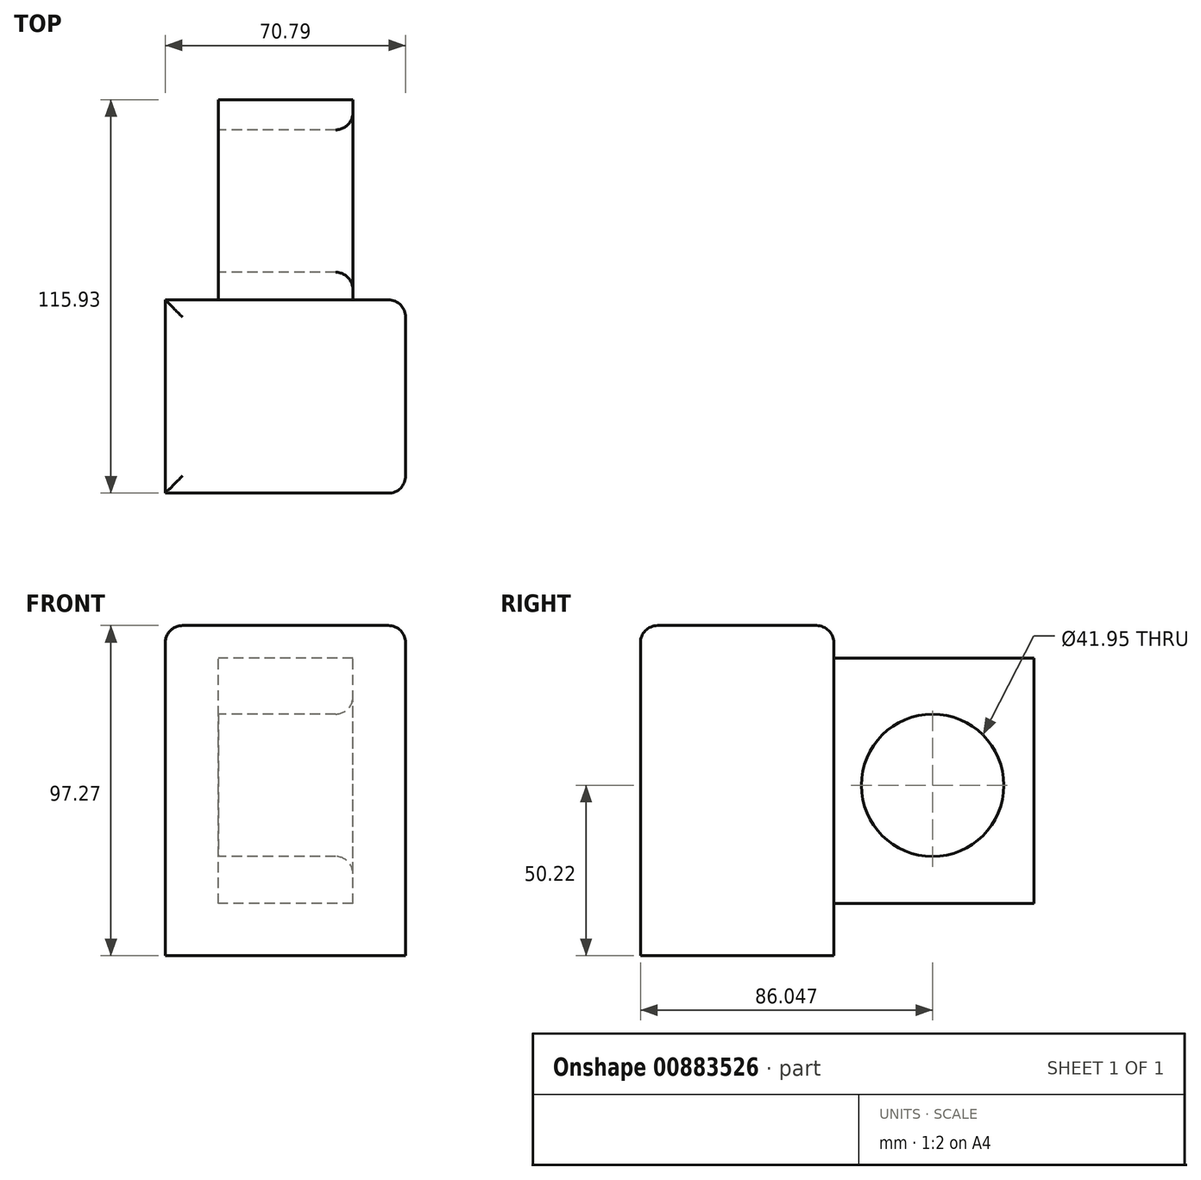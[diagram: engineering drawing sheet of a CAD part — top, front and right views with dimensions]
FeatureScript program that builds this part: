
annotation { "Feature Type Name" : "Feature", "Feature Type Description" : "" }
export const myFeature = defineFeature(function(context is Context, id is Id, definition is map)
    precondition{}
    {
        {
            var Q0;
            Q0=qCreatedBy(makeId("Top.planeOp"),FACE);
            var sketch = newSketch(context, id + "F0", { "sketchPlane" : qUnion([Q0])});
            skLineSegment(sketch, "E0.bottom", {"start": v(16.2, 0) * mm, "end": v(87, 0) * mm});
            skLineSegment(sketch, "E0.top", {"start": v(16.2, 56.94) * mm, "end": v(87, 56.94) * mm});
            skLineSegment(sketch, "E0.left", {"start": v(16.2, 0) * mm, "end": v(16.2, 56.94) * mm});
            skLineSegment(sketch, "E0.right", {"start": v(87, 0) * mm, "end": v(87, 56.94) * mm});
            skPoint(sketch, "E0.middle", {"position": v(51.6, 28.47) * mm});
            skSolve(sketch);
        }
        {
            var Q0;
            Q0=makeQuery(id+"F0.imprint","IMPRINT",FACE,{"disambiguationData":[TD([[makeQuery(id+"F0.imprint","IMPRINT",EDGE,{"derivedFrom":sQuery(id+"F0.wireOp",EDGE,"E0.bottom")}),1.0]])]});
            extrude(context, id + "F1", {"entities" : qUnion([Q0]), "depth" : 97.27 * mm, "offsetDistance" : 25.4 * mm});
        }
        {
            var Q0;
            Q0=makeQuery(id+"F1.opExtrude","CAP_EDGE",EDGE,{"disambiguationData":[OSD([sQuery(id+"F0.wireOp",EDGE,"E0.right")])],"isStart":false});
            fillet(context, id + "F2", {"entities" : qUnion([Q0]), "radius" : 5.08 * mm, "tangentPropagation" : true, "allowEdgeOverflow" : false});
        }
        {
            var Q0;
            Q0=makeQuery(id+"F1.opExtrude","CAP_EDGE",EDGE,{"disambiguationData":[OSD([sQuery(id+"F0.wireOp",EDGE,"E0.left")])],"isStart":false});
            var Q1;
            Q1=makeQuery(id+"F1.opExtrude","CAP_EDGE",EDGE,{"disambiguationData":[OSD([sQuery(id+"F0.wireOp",EDGE,"E0.bottom")])],"isStart":false});
            var Q2;
            Q2=makeQuery(id+"F1.opExtrude","CAP_EDGE",EDGE,{"disambiguationData":[OSD([sQuery(id+"F0.wireOp",EDGE,"E0.top")])],"isStart":false});
            fillet(context, id + "F3", {"entities" : qUnion([Q0, Q1, Q2]), "radius" : 5.08 * mm, "tangentPropagation" : true, "allowEdgeOverflow" : false});
        }
        {
            var Q0;
            Q0=makeQuery(id+"F1.opExtrude","SWEPT_FACE",FACE,{"disambiguationData":[OSD([sQuery(id+"F0.wireOp",EDGE,"E0.top")])]});
            var sketch = newSketch(context, id + "F4", { "sketchPlane" : qUnion([Q0])});
            skLineSegment(sketch, "E1.bottom", {"start": v(-71.47, 15.38) * mm, "end": v(-31.89, 15.38) * mm});
            skLineSegment(sketch, "E1.top", {"start": v(-71.47, 87.71) * mm, "end": v(-31.89, 87.71) * mm});
            skLineSegment(sketch, "E1.left", {"start": v(-71.47, 15.38) * mm, "end": v(-71.47, 87.71) * mm});
            skLineSegment(sketch, "E1.right", {"start": v(-31.89, 15.38) * mm, "end": v(-31.89, 87.71) * mm});
            skPoint(sketch, "E1.middle", {"position": v(-51.68, 51.55) * mm});
            skSolve(sketch);
        }
        {
            var Q0;
            Q0=makeQuery(id+"F4.imprint","IMPRINT",FACE,{"disambiguationData":[TD([[makeQuery(id+"F4.imprint","IMPRINT",EDGE,{"derivedFrom":sQuery(id+"F4.wireOp",EDGE,"E1.bottom")}),1.0]])]});
            extrude(context, id + "F5", {"entities" : qUnion([Q0]), "operationType" : NewBodyOperationType.ADD, "depth" : 59 * mm, "offsetDistance" : 25.4 * mm});
        }
        {
            var Q0;
            Q0=makeQuery(id+"F5.opExtrude","SWEPT_FACE",FACE,{"disambiguationData":[OSD([sQuery(id+"F4.wireOp",EDGE,"E1.right")])]});
            var sketch = newSketch(context, id + "F6", { "sketchPlane" : qUnion([Q0])});
            skCircle(sketch, "E2", {"center": v(-86.05, 50.22) * mm, "radius": 20.98 * mm});
            skSolve(sketch);
        }
        {
            var Q0;
            Q0=makeQuery(id+"F6.imprint","IMPRINT",FACE,{"disambiguationData":[TD([[makeQuery(id+"F6.imprint","IMPRINT",EDGE,{"derivedFrom":sQuery(id+"F6.wireOp",EDGE,"E2")}),1.0]])]});
            extrude(context, id + "F7", {"entities" : qUnion([Q0]), "operationType" : NewBodyOperationType.REMOVE, "oppositeDirection" : true, "depth" : 77.68 * mm, "offsetDistance" : 25.4 * mm});
        }
        {
            var Q0;
            Q0=makeQuery(id+"F7.boolean.opBoolean","INTERSECT",EDGE,{"derivedFrom":[makeQuery(id+"F5.opExtrude","SWEPT_FACE",FACE,{"disambiguationData":[OSD([sQuery(id+"F4.wireOp",EDGE,"E1.left")])]}),makeQuery(id+"F7.opExtrude","SWEPT_FACE",FACE,{"disambiguationData":[OSD([sQuery(id+"F6.wireOp",EDGE,"E2")])]})]});
            var Q1;
            Q1=makeQuery(id+"F7.boolean.opBoolean","COPY",EDGE,{"derivedFrom":makeQuery(id+"F7.opExtrude","CAP_EDGE",EDGE,{"disambiguationData":[OSD([sQuery(id+"F6.wireOp",EDGE,"E2")])],"isStart":true})});
            fillet(context, id + "F8", {"entities" : qUnion([Q0, Q1]), "radius" : 5.08 * mm, "tangentPropagation" : true, "allowEdgeOverflow" : false});
        }
    });
